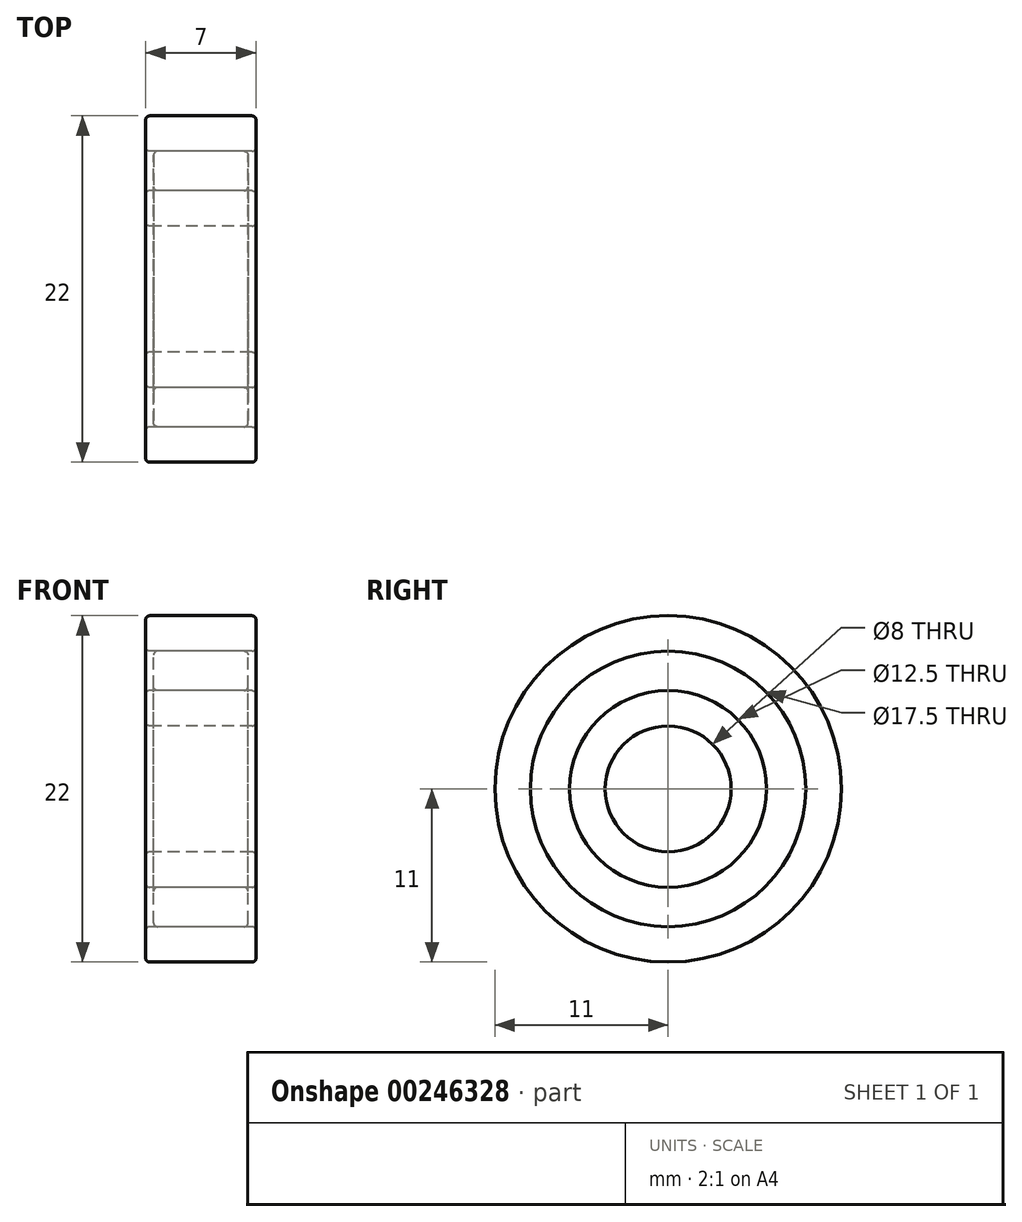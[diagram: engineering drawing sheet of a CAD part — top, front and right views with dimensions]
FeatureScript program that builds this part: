
annotation { "Feature Type Name" : "Feature", "Feature Type Description" : "" }
export const myFeature = defineFeature(function(context is Context, id is Id, definition is map)
    precondition{}
    {
        {
            var Q0;
            Q0=qCreatedBy(makeId("Right.planeOp"),FACE);
            var sketch = newSketch(context, id + "F0", { "sketchPlane" : qUnion([Q0])});
            skCircle(sketch, "E0", {"center": v(0, 0) * mm, "radius": 11 * mm});
            skCircle(sketch, "E1", {"center": v(0, 0) * mm, "radius": 8.75 * mm});
            skSolve(sketch);
        }
        {
            var Q0;
            Q0=makeQuery(id+"F0.imprint","IMPRINT",FACE,{"disambiguationData":[TD([[makeQuery(id+"F0.imprint","IMPRINT",EDGE,{"derivedFrom":sQuery(id+"F0.wireOp",EDGE,"E0")}),1.0]])]});
            var Q1;
            Q1=sQuery(id+"F0.wireOp",EDGE,"E0");
            extrude(context, id + "F1", {"entities" : qUnion([Q0]), "surfaceEntities" : qUnion([Q1]), "depth" : 7 * mm, "offsetDistance" : 25 * mm, "symmetric" : true});
        }
        {
            var Q0;
            Q0=makeQuery(id+"F1.opExtrude","SWEPT_FACE",FACE,{"disambiguationData":[OSD([sQuery(id+"F0.wireOp",EDGE,"E0")])]});
            var Q1;
            Q1=makeQuery(id+"F1.opExtrude","CAP_EDGE",EDGE,{"disambiguationData":[OSD([sQuery(id+"F0.wireOp",EDGE,"E1")])],"isStart":false});
            fillet(context, id + "F2", {"entities" : qUnion([Q0, Q1]), "radius" : 0.25 * mm, "tangentPropagation" : true, "allowEdgeOverflow" : false});
        }
        {
            var Q0;
            Q0=makeQuery(id+"F1.opExtrude","SWEPT_FACE",FACE,{"disambiguationData":[OSD([sQuery(id+"F0.wireOp",EDGE,"E1")])]});
            fillet(context, id + "F3", {"entities" : qUnion([Q0]), "radius" : 0.25 * mm, "tangentPropagation" : true, "allowEdgeOverflow" : false});
        }
        {
            var Q0;
            Q0=qCreatedBy(makeId("Right.planeOp"),FACE);
            var sketch = newSketch(context, id + "F4", { "sketchPlane" : qUnion([Q0])});
            skCircle(sketch, "E2", {"center": v(0, 0) * mm, "radius": 6.25 * mm});
            skCircle(sketch, "E3", {"center": v(0, 0) * mm, "radius": 4 * mm});
            skSolve(sketch);
        }
        {
            var Q0;
            Q0 = qSketchRegion(id + "F4", true);
            extrude(context, id + "F5", {"entities" : qUnion([Q0]), "depth" : 7 * mm, "offsetDistance" : 25 * mm, "symmetric" : true});
        }
        {
            var Q0;
            Q0=makeQuery(id+"F5.opExtrude","SWEPT_FACE",FACE,{"disambiguationData":[OSD([sQuery(id+"F4.wireOp",EDGE,"E3")])]});
            fillet(context, id + "F6", {"entities" : qUnion([Q0]), "radius" : 0.25 * mm, "tangentPropagation" : true, "allowEdgeOverflow" : false});
        }
        {
            var Q0;
            Q0=makeQuery(id+"F5.opExtrude","SWEPT_FACE",FACE,{"disambiguationData":[OSD([sQuery(id+"F4.wireOp",EDGE,"E2")])]});
            fillet(context, id + "F7", {"entities" : qUnion([Q0]), "radius" : 0.25 * mm, "tangentPropagation" : true, "allowEdgeOverflow" : false});
        }
        {
            var Q0;
            Q0=qCreatedBy(makeId("Right.planeOp"),FACE);
            var sketch = newSketch(context, id + "F8", { "sketchPlane" : qUnion([Q0])});
            skCircle(sketch, "E4", {"center": v(0, 0) * mm, "radius": 8.75 * mm});
            skCircle(sketch, "E5", {"center": v(0, 0) * mm, "radius": 6.25 * mm});
            skSolve(sketch);
        }
        {
            var Q0;
            Q0 = qSketchRegion(id + "F8", true);
            extrude(context, id + "F9", {"entities" : qUnion([Q0]), "depth" : 6 * mm, "offsetDistance" : 25 * mm, "symmetric" : true});
        }
        {
            var Q0;
            Q0=makeQuery(id+"F9.opExtrude","SWEPT_FACE",FACE,{"disambiguationData":[OSD([sQuery(id+"F8.wireOp",EDGE,"E5")])]});
            fillet(context, id + "F10", {"entities" : qUnion([Q0]), "radius" : 0.25 * mm, "tangentPropagation" : true, "allowEdgeOverflow" : false});
        }
        {
            var Q0;
            Q0=makeQuery(id+"F9.opExtrude","SWEPT_FACE",FACE,{"disambiguationData":[OSD([sQuery(id+"F8.wireOp",EDGE,"E4")])]});
            fillet(context, id + "F11", {"entities" : qUnion([Q0]), "radius" : 0.25 * mm, "tangentPropagation" : true, "allowEdgeOverflow" : false});
        }
    });
